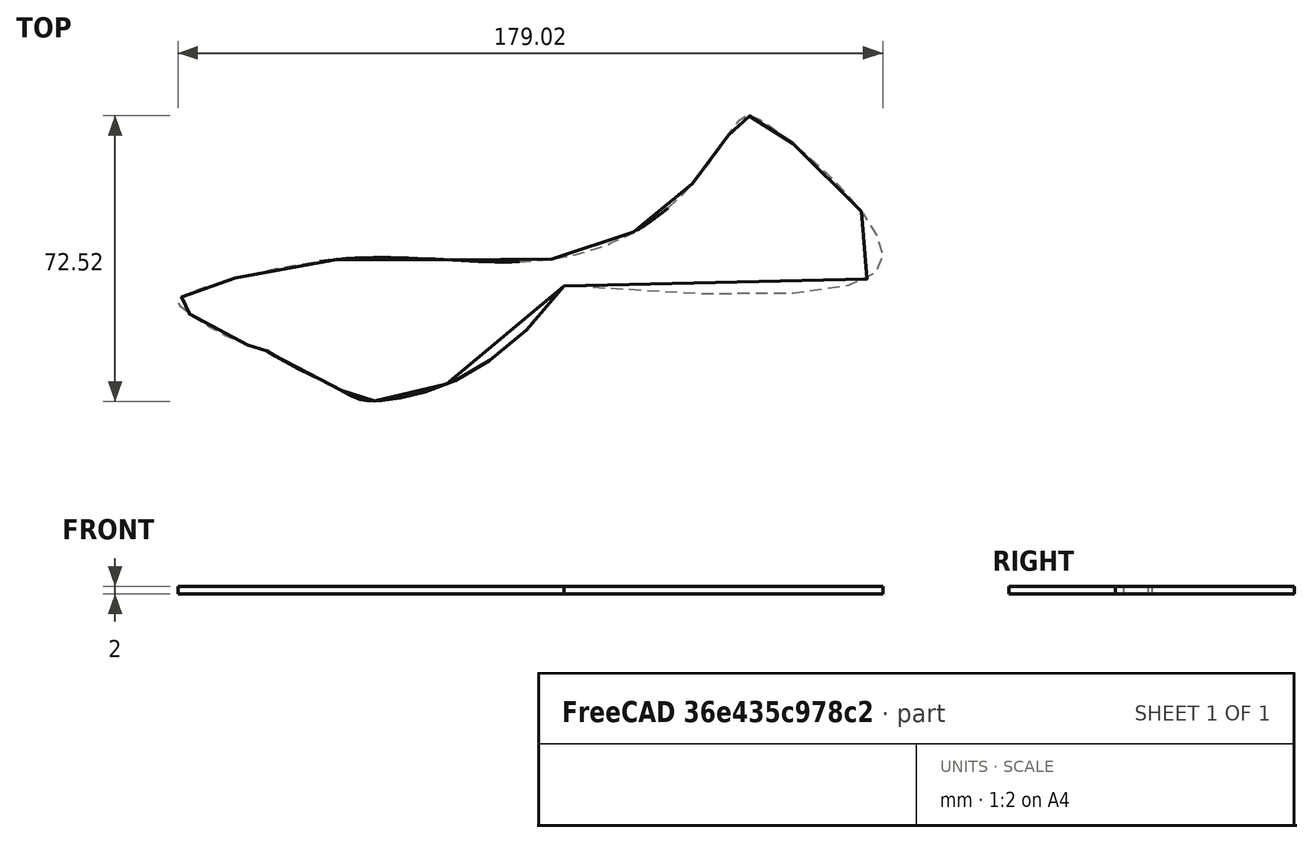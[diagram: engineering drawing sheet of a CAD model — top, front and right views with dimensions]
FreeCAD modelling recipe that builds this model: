
FCSTD DOCUMENT  (FreeCAD 0.18R16110 (Git))
Label: wingtop
License: All rights reserved
LicenseURL: http://en.wikipedia.org/wiki/All_rights_reserved
objects: Sketcher::SketchObject×2, PartDesign::Pad×1, PartDesign::Body×1
note: 5 computed .brp shape members not serialized (recipe doc carries the construction recipe); baked Part::Feature solids carry a one-line shape summary decoded from their .brp

FEATURE [Sketcher::SketchObject] Sketch001
  sketch-geometry (35):
    g0: LineSegment [constr] StartX=-100 StartY=0 StartZ=0 EndX=100 EndY=0 EndZ=0
    g1: LineSegment [constr] StartX=100 StartY=0 StartZ=0 EndX=50.5 EndY=49.5 EndZ=0
    g2: LineSegment [constr] StartX=50.5 StartY=49.5 StartZ=0 EndX=50.5 EndY=0 EndZ=0
    g3-g18: Circle [constr] x16 (B-spline internal-alignment scaffolding for g19; pole/knot coordinates omitted)
    g19: BSplineCurve PolesCount=17 KnotsCount=15 Degree=3 IsPeriodic=0
    g20-g34: GeomPoint [constr] x15 (B-spline internal-alignment scaffolding for g19; pole/knot coordinates omitted)
  constraints (14):
    c: PointOnObject(g0,g-1)
    c: PointOnObject(g0,g-1)
    c: Coincident(g1,g0)
    c: Angle(g1,g0) = 0.785398
    c: PointOnObject(g2,g0)
    c: Vertical(g2)
    c: Coincident(g1,g2)
    c: Radius(g3) = 5
    c: Equal(g3, g4-g8) x5
    c: PointOnObject(g8,g0)
    c: Equal(g3, g9-g18) x10
    c: InternalAlignment(g3-g18 -> g19) x16
    c: InternalAlignment(g20-g34 -> g19) x15
    c: PointOnObject(g22,g19)
FEATURE [Sketcher::SketchObject] CopySketch001
  sketch-geometry (35):
    g0: LineSegment [constr] StartX=-100 StartY=0 StartZ=0 EndX=100 EndY=0 EndZ=0
    g1: LineSegment [constr] StartX=100 StartY=0 StartZ=0 EndX=50.5 EndY=49.5 EndZ=0
    g2: LineSegment [constr] StartX=50.5 StartY=49.5 StartZ=0 EndX=50.5 EndY=0 EndZ=0
    g3-g18: Circle [constr] x16 (B-spline internal-alignment scaffolding for g19; pole/knot coordinates omitted)
    g19: BSplineCurve PolesCount=17 KnotsCount=15 Degree=3 IsPeriodic=0
    g20-g34: GeomPoint [constr] x15 (B-spline internal-alignment scaffolding for g19; pole/knot coordinates omitted)
  constraints (14):
    c: PointOnObject(g0,g-1)
    c: PointOnObject(g0,g-1)
    c: Coincident(g1,g0)
    c: Angle(g1,g0) = 0.785398
    c: PointOnObject(g2,g0)
    c: Vertical(g2)
    c: Coincident(g1,g2)
    c: Radius(g3) = 5
    c: Equal(g3, g4-g8) x5
    c: PointOnObject(g8,g0)
    c: Equal(g3, g9-g18) x10
    c: InternalAlignment(g3-g18 -> g19) x16
    c: InternalAlignment(g20-g34 -> g19) x15
    c: PointOnObject(g22,g19)
FEATURE [PartDesign::Pad] Pad
  Length = 2
  Length2 = 100
  Profile = -> CopySketch001
  Type = 0
FEATURE [PartDesign::Body] Body001
  Group = -> [Pad]
  Origin = -> Origin001
  Tip = -> Pad
